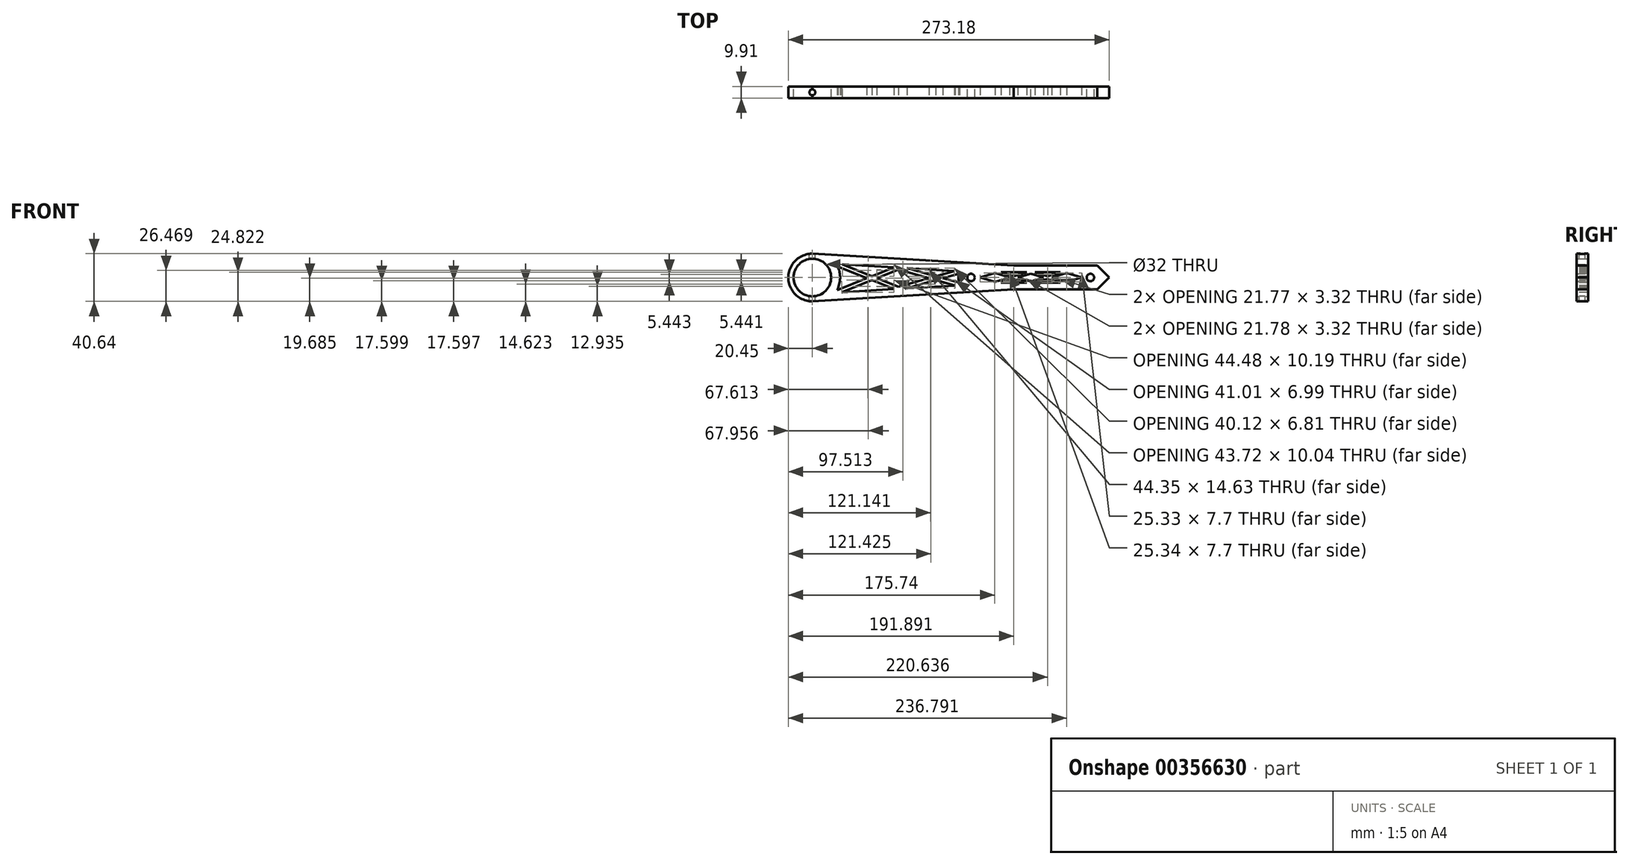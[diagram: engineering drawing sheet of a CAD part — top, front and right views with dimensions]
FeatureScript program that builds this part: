
annotation { "Feature Type Name" : "Feature", "Feature Type Description" : "" }
export const myFeature = defineFeature(function(context is Context, id is Id, definition is map)
    precondition{}
    {
        {
            var Q0;
            Q0=qCreatedBy(makeId("Front.planeOp"),FACE);
            var sketch = newSketch(context, id + "F0", { "sketchPlane" : qUnion([Q0])});
            skLineSegment(sketch, "E0.bottom", {"start": v(40.64, -10.16) * mm, "end": v(-40.64, -10.16) * mm});
            skLineSegment(sketch, "E0.top", {"start": v(40.64, 10.16) * mm, "end": v(-40.64, 10.16) * mm});
            skLineSegment(sketch, "E0.left", {"start": v(40.64, -10.16) * mm, "end": v(40.64, 10.16) * mm});
            skPoint(sketch, "E0.middle", {"position": v(0, 0) * mm});
            skLineSegment(sketch, "E1.bottom", {"start": v(-212.1, -20.32) * mm, "end": v(-212.36, -20.32) * mm});
            skLineSegment(sketch, "E1.top", {"start": v(-212.09, 20.32) * mm, "end": v(-212.36, 20.32) * mm});
            skLineSegment(sketch, "E1.right", {"start": v(-232.4, -2.34) * mm, "end": v(-232.4, 2.34) * mm});
            skPoint(sketch, "E1.middle", {"position": v(-212.1, 0) * mm});
            skCircle(sketch, "E2", {"center": v(-212.1, 0) * mm, "radius": 16 * mm});
            skArc(sketch, "E3", {"start": v(-212.09, 20.32) * mm, "mid": v(-232.54, 0) * mm, "end": v(-212.1, -20.32) * mm});
            skPoint(sketch, "E4.orphan", {"position": v(-232.4, 20.32) * mm});
            skPoint(sketch, "E5.orphan", {"position": v(-232.4, -20.32) * mm});
            skCircle(sketch, "E6", {"center": v(-77.09, 0) * mm, "radius": 3.18 * mm});
            skCircle(sketch, "E7", {"center": v(24.54, 0) * mm, "radius": 3.18 * mm});
            skLineSegment(sketch, "E8", {"start": v(-212.1, -20.32) * mm, "end": v(-40.64, -10.16) * mm});
            skLineSegment(sketch, "E9", {"start": v(-212.09, 20.32) * mm, "end": v(-40.64, 10.16) * mm});
            skLineSegment(sketch, "E10", {"start": v(-212.09, 31.09) * mm, "end": v(-212.09, -33.26) * mm, "construction": true});
            skSolve(sketch);
        }
        {
            var Q0;
            Q0 = qSketchRegion(id + "F0", true);
            extrude(context, id + "F1", {"entities" : qUnion([Q0]), "depth" : 9.9 * mm});
        }
        {
            var Q0;
            Q0=makeQuery(id+"F1.opExtrude","CAP_FACE",FACE,{"disambiguationData":[OSD([sQuery(id+"F0.wireOp",EDGE,"E0.bottom"),sQuery(id+"F0.wireOp",EDGE,"E0.top"),sQuery(id+"F0.wireOp",EDGE,"E0.left"),sQuery(id+"F0.wireOp",EDGE,"E2"),sQuery(id+"F0.wireOp",EDGE,"E3"),sQuery(id+"F0.wireOp",EDGE,"E6"),sQuery(id+"F0.wireOp",EDGE,"E7"),sQuery(id+"F0.wireOp",EDGE,"E8"),sQuery(id+"F0.wireOp",EDGE,"E9")])],"isStart":false});
            var sketch = newSketch(context, id + "F2", { "sketchPlane" : qUnion([Q0])});
            skArc(sketch, "E11.0", {"start": v(-192.22, -12.78) * mm, "mid": v(-188.48, -0.77) * mm, "end": v(-191.44, 11.46) * mm});
            skArc(sketch, "E12.0", {"start": v(-86.52, 5.25) * mm, "mid": v(-87.86, -0.73) * mm, "end": v(-85.73, -6.47) * mm});
            skLineSegment(sketch, "E13.0", {"start": v(-191.44, 11.46) * mm, "end": v(-86.52, 5.25) * mm});
            skLineSegment(sketch, "E14.0", {"start": v(-192.22, -12.78) * mm, "end": v(-85.73, -6.47) * mm});
            skSolve(sketch);
        }
        {
            var Q0;
            Q0 = qSketchRegion(id + "F2", true);
            extrude(context, id + "F3", {"entities" : qUnion([Q0]), "operationType" : NewBodyOperationType.REMOVE, "endBound" : BoundingType.THROUGH_ALL, "oppositeDirection" : true, "depth" : 25.4 * mm});
        }
        {
            var Q0;
            Q0=makeQuery(id+"F1.opExtrude","CAP_FACE",FACE,{"disambiguationData":[OSD([sQuery(id+"F0.wireOp",EDGE,"E0.bottom"),sQuery(id+"F0.wireOp",EDGE,"E0.top"),sQuery(id+"F0.wireOp",EDGE,"E0.left"),sQuery(id+"F0.wireOp",EDGE,"E2"),sQuery(id+"F0.wireOp",EDGE,"E3"),sQuery(id+"F0.wireOp",EDGE,"E6"),sQuery(id+"F0.wireOp",EDGE,"E7"),sQuery(id+"F0.wireOp",EDGE,"E8"),sQuery(id+"F0.wireOp",EDGE,"E9")])],"isStart":false});
            var sketch = newSketch(context, id + "F4", { "sketchPlane" : qUnion([Q0])});
            skLineSegment(sketch, "E15", {"start": v(-191.44, 11.46) * mm, "end": v(-138.98, -9.63) * mm});
            skLineSegment(sketch, "E16", {"start": v(-138.98, -9.63) * mm, "end": v(-86.52, 5.25) * mm});
            skLineSegment(sketch, "E17", {"start": v(-85.73, -6.47) * mm, "end": v(-138.98, 8.35) * mm});
            skLineSegment(sketch, "E18", {"start": v(-138.98, 8.35) * mm, "end": v(-192.22, -12.78) * mm});
            skLineSegment(sketch, "E19.0", {"start": v(-190.84, 12.94) * mm, "end": v(-138.39, -8.15) * mm});
            skLineSegment(sketch, "E20.0", {"start": v(-192.03, 9.99) * mm, "end": v(-139.57, -11.1) * mm});
            skLineSegment(sketch, "E21.0", {"start": v(-139.57, 9.83) * mm, "end": v(-192.81, -11.3) * mm});
            skLineSegment(sketch, "E22.0", {"start": v(-138.4, 6.88) * mm, "end": v(-191.64, -14.26) * mm});
            skLineSegment(sketch, "E23.0", {"start": v(-85.3, -4.94) * mm, "end": v(-138.55, 9.88) * mm});
            skLineSegment(sketch, "E24.0", {"start": v(-86.16, -8) * mm, "end": v(-139.4, 6.82) * mm});
            skLineSegment(sketch, "E25.0", {"start": v(-138.54, -11.15) * mm, "end": v(-86.1, 3.72) * mm});
            skLineSegment(sketch, "E26.0", {"start": v(-139.41, -8.1) * mm, "end": v(-86.96, 6.77) * mm});
            skLineSegment(sketch, "E27", {"start": v(-192.03, 9.99) * mm, "end": v(-190.84, 12.94) * mm});
            skSolve(sketch);
        }
        {
            var Q0;
            {var subQ0=sQuery(id+"F4.wireOp",EDGE,"E21.0");var subQ1=sQuery(id+"F4.wireOp",EDGE,"E15");var subQ2=makeQuery(id+"F4.imprint","INTERSECT",VERTEX,{"derivedFrom":[subQ1,subQ0]});Q0=makeQuery(id+"F4.imprint","IMPRINT",FACE,{"disambiguationData":[TD([[makeQuery(id+"F4.imprint","IMPRINT",EDGE,{"disambiguationData":[TD([[subQ2,-1.0]])],"derivedFrom":subQ1}),1.0]])]});}
            var Q1;
            {var subQ0=sQuery(id+"F4.wireOp",EDGE,"E21.0");var subQ1=sQuery(id+"F4.wireOp",EDGE,"E15");var subQ2=makeQuery(id+"F4.imprint","INTERSECT",VERTEX,{"derivedFrom":[subQ1,subQ0]});Q1=makeQuery(id+"F4.imprint","IMPRINT",FACE,{"disambiguationData":[TD([[makeQuery(id+"F4.imprint","IMPRINT",EDGE,{"disambiguationData":[TD([[subQ2,-1.0]])],"derivedFrom":subQ1}),-1.0]])]});}
            var Q2;
            {var subQ0=sQuery(id+"F4.wireOp",EDGE,"E18");var subQ1=sQuery(id+"F4.wireOp",EDGE,"E15");var subQ2=makeQuery(id+"F4.imprint","INTERSECT",VERTEX,{"derivedFrom":[subQ1,subQ0]});Q2=makeQuery(id+"F4.imprint","IMPRINT",FACE,{"disambiguationData":[TD([[makeQuery(id+"F4.imprint","IMPRINT",EDGE,{"disambiguationData":[TD([[subQ2,-1.0]])],"derivedFrom":subQ1}),1.0]])]});}
            var Q3;
            {var subQ0=sQuery(id+"F4.wireOp",EDGE,"E18");var subQ1=sQuery(id+"F4.wireOp",EDGE,"E15");var subQ2=makeQuery(id+"F4.imprint","INTERSECT",VERTEX,{"derivedFrom":[subQ1,subQ0]});Q3=makeQuery(id+"F4.imprint","IMPRINT",FACE,{"disambiguationData":[TD([[makeQuery(id+"F4.imprint","IMPRINT",EDGE,{"disambiguationData":[TD([[subQ2,-1.0]])],"derivedFrom":subQ1}),-1.0]])]});}
            var Q4;
            {var subQ0=sQuery(id+"F4.wireOp",EDGE,"E24.0");var subQ1=sQuery(id+"F4.wireOp",EDGE,"E16");var subQ2=makeQuery(id+"F4.imprint","INTERSECT",VERTEX,{"derivedFrom":[subQ1,subQ0]});Q4=makeQuery(id+"F4.imprint","IMPRINT",FACE,{"disambiguationData":[TD([[makeQuery(id+"F4.imprint","IMPRINT",EDGE,{"disambiguationData":[TD([[subQ2,-1.0]])],"derivedFrom":subQ1}),-1.0]])]});}
            var Q5;
            {var subQ0=sQuery(id+"F4.wireOp",EDGE,"E24.0");var subQ1=sQuery(id+"F4.wireOp",EDGE,"E16");var subQ2=makeQuery(id+"F4.imprint","INTERSECT",VERTEX,{"derivedFrom":[subQ1,subQ0]});Q5=makeQuery(id+"F4.imprint","IMPRINT",FACE,{"disambiguationData":[TD([[makeQuery(id+"F4.imprint","IMPRINT",EDGE,{"disambiguationData":[TD([[subQ2,-1.0]])],"derivedFrom":subQ1}),1.0]])]});}
            var Q6;
            {var subQ0=sQuery(id+"F4.wireOp",EDGE,"E17");var subQ1=sQuery(id+"F4.wireOp",EDGE,"E16");var subQ2=makeQuery(id+"F4.imprint","INTERSECT",VERTEX,{"derivedFrom":[subQ1,subQ0]});Q6=makeQuery(id+"F4.imprint","IMPRINT",FACE,{"disambiguationData":[TD([[makeQuery(id+"F4.imprint","IMPRINT",EDGE,{"disambiguationData":[TD([[subQ2,-1.0]])],"derivedFrom":subQ1}),-1.0]])]});}
            var Q7;
            {var subQ0=sQuery(id+"F4.wireOp",EDGE,"E17");var subQ1=sQuery(id+"F4.wireOp",EDGE,"E16");var subQ2=makeQuery(id+"F4.imprint","INTERSECT",VERTEX,{"derivedFrom":[subQ1,subQ0]});Q7=makeQuery(id+"F4.imprint","IMPRINT",FACE,{"disambiguationData":[TD([[makeQuery(id+"F4.imprint","IMPRINT",EDGE,{"disambiguationData":[TD([[subQ2,-1.0]])],"derivedFrom":subQ1}),1.0]])]});}
            var Q8;
            {var subQ3=sQuery(id+"F4.wireOp",EDGE,"E19.0");var subQ5=sQuery(id+"F4.wireOp",EDGE,"E26.0");var subQ6=makeQuery(id+"F4.imprint","INTERSECT",VERTEX,{"derivedFrom":[subQ3,subQ5]});Q8=makeQuery(id+"F4.imprint","IMPRINT",FACE,{"disambiguationData":[TD([[makeQuery(id+"F4.imprint","IMPRINT",EDGE,{"disambiguationData":[TD([[subQ6,1.0]])],"derivedFrom":subQ3}),-1.0]])]});}
            var Q9;
            {var subQ3=sQuery(id+"F4.wireOp",EDGE,"E19.0");var subQ5=sQuery(id+"F4.wireOp",EDGE,"E18");var subQ6=makeQuery(id+"F4.imprint","INTERSECT",VERTEX,{"derivedFrom":[subQ5,subQ3]});Q9=makeQuery(id+"F4.imprint","IMPRINT",FACE,{"disambiguationData":[TD([[makeQuery(id+"F4.imprint","IMPRINT",EDGE,{"disambiguationData":[TD([[subQ6,-1.0]])],"derivedFrom":subQ3}),1.0]])]});}
            var Q10;
            {var subQ0=sQuery(id+"F4.wireOp",EDGE,"E27");var subQ1=sQuery(id+"F4.wireOp",EDGE,"E19.0");var subQ2=makeQuery(id+"F4.imprint","INTERSECT",VERTEX,{"derivedFrom":[subQ1,subQ0]});Q10=makeQuery(id+"F4.imprint","IMPRINT",FACE,{"disambiguationData":[TD([[makeQuery(id+"F4.imprint","IMPRINT",EDGE,{"disambiguationData":[TD([[subQ2,-1.0]])],"derivedFrom":subQ1}),-1.0]])]});}
            var Q11;
            {var subQ0=sQuery(id+"F4.wireOp",EDGE,"E27");var subQ1=sQuery(id+"F4.wireOp",EDGE,"E20.0");var subQ2=makeQuery(id+"F4.imprint","INTERSECT",VERTEX,{"derivedFrom":[subQ1,subQ0]});Q11=makeQuery(id+"F4.imprint","IMPRINT",FACE,{"disambiguationData":[TD([[makeQuery(id+"F4.imprint","IMPRINT",EDGE,{"disambiguationData":[TD([[subQ2,-1.0]])],"derivedFrom":subQ1}),1.0]])]});}
            var Q12;
            {var subQ3=sQuery(id+"F4.wireOp",EDGE,"E21.0");var subQ5=sQuery(id+"F4.wireOp",EDGE,"E19.0");var subQ6=makeQuery(id+"F4.imprint","INTERSECT",VERTEX,{"derivedFrom":[subQ5,subQ3]});Q12=makeQuery(id+"F4.imprint","IMPRINT",FACE,{"disambiguationData":[TD([[makeQuery(id+"F4.imprint","IMPRINT",EDGE,{"disambiguationData":[TD([[subQ6,1.0]])],"derivedFrom":subQ5}),-1.0]])]});}
            var Q13;
            {var subQ0=sQuery(id+"F4.wireOp",EDGE,"E18");var subQ3=sQuery(id+"F4.wireOp",EDGE,"E20.0");var subQ4=makeQuery(id+"F4.imprint","INTERSECT",VERTEX,{"derivedFrom":[subQ0,subQ3]});Q13=makeQuery(id+"F4.imprint","IMPRINT",FACE,{"disambiguationData":[TD([[makeQuery(id+"F4.imprint","IMPRINT",EDGE,{"disambiguationData":[TD([[subQ4,1.0]])],"derivedFrom":subQ3}),-1.0]])]});}
            var Q14;
            {var subQ0=sQuery(id+"F4.wireOp",EDGE,"E18");var subQ3=sQuery(id+"F4.wireOp",EDGE,"E20.0");var subQ4=makeQuery(id+"F4.imprint","INTERSECT",VERTEX,{"derivedFrom":[subQ0,subQ3]});Q14=makeQuery(id+"F4.imprint","IMPRINT",FACE,{"disambiguationData":[TD([[makeQuery(id+"F4.imprint","IMPRINT",EDGE,{"disambiguationData":[TD([[subQ4,-1.0]])],"derivedFrom":subQ3}),-1.0]])]});}
            var Q15;
            {var subQ3=sQuery(id+"F4.wireOp",EDGE,"E26.0");var subQ5=sQuery(id+"F4.wireOp",EDGE,"E23.0");var subQ6=makeQuery(id+"F4.imprint","INTERSECT",VERTEX,{"derivedFrom":[subQ5,subQ3]});Q15=makeQuery(id+"F4.imprint","IMPRINT",FACE,{"disambiguationData":[TD([[makeQuery(id+"F4.imprint","IMPRINT",EDGE,{"disambiguationData":[TD([[subQ6,-1.0]])],"derivedFrom":subQ5}),1.0]])]});}
            var Q16;
            {var subQ0=sQuery(id+"F4.wireOp",EDGE,"E18");var subQ3=sQuery(id+"F4.wireOp",EDGE,"E19.0");var subQ4=makeQuery(id+"F4.imprint","INTERSECT",VERTEX,{"derivedFrom":[subQ0,subQ3]});Q16=makeQuery(id+"F4.imprint","IMPRINT",FACE,{"disambiguationData":[TD([[makeQuery(id+"F4.imprint","IMPRINT",EDGE,{"disambiguationData":[TD([[subQ4,1.0]])],"derivedFrom":subQ3}),1.0]])]});}
            var Q17;
            {var subQ0=sQuery(id+"F4.wireOp",EDGE,"E16");var subQ3=sQuery(id+"F4.wireOp",EDGE,"E23.0");var subQ4=makeQuery(id+"F4.imprint","INTERSECT",VERTEX,{"derivedFrom":[subQ0,subQ3]});Q17=makeQuery(id+"F4.imprint","IMPRINT",FACE,{"disambiguationData":[TD([[makeQuery(id+"F4.imprint","IMPRINT",EDGE,{"disambiguationData":[TD([[subQ4,1.0]])],"derivedFrom":subQ3}),-1.0]])]});}
            var Q18;
            {var subQ0=sQuery(id+"F4.wireOp",EDGE,"E16");var subQ3=sQuery(id+"F4.wireOp",EDGE,"E23.0");var subQ4=makeQuery(id+"F4.imprint","INTERSECT",VERTEX,{"derivedFrom":[subQ0,subQ3]});Q18=makeQuery(id+"F4.imprint","IMPRINT",FACE,{"disambiguationData":[TD([[makeQuery(id+"F4.imprint","IMPRINT",EDGE,{"disambiguationData":[TD([[subQ4,-1.0]])],"derivedFrom":subQ3}),-1.0]])]});}
            var Q19;
            {var subQ3=sQuery(id+"F4.wireOp",EDGE,"E25.0");var subQ5=sQuery(id+"F4.wireOp",EDGE,"E23.0");var subQ6=makeQuery(id+"F4.imprint","INTERSECT",VERTEX,{"derivedFrom":[subQ5,subQ3]});Q19=makeQuery(id+"F4.imprint","IMPRINT",FACE,{"disambiguationData":[TD([[makeQuery(id+"F4.imprint","IMPRINT",EDGE,{"disambiguationData":[TD([[subQ6,1.0]])],"derivedFrom":subQ5}),1.0]])]});}
            var Q20;
            {var subQ3=sQuery(id+"F4.wireOp",EDGE,"E25.0");var subQ5=sQuery(id+"F4.wireOp",EDGE,"E24.0");var subQ6=makeQuery(id+"F4.imprint","INTERSECT",VERTEX,{"derivedFrom":[subQ5,subQ3]});Q20=makeQuery(id+"F4.imprint","IMPRINT",FACE,{"disambiguationData":[TD([[makeQuery(id+"F4.imprint","IMPRINT",EDGE,{"disambiguationData":[TD([[subQ6,1.0]])],"derivedFrom":subQ5}),-1.0]])]});}
            var Q21;
            {var subQ0=sQuery(id+"F4.wireOp",EDGE,"E16");var subQ3=sQuery(id+"F4.wireOp",EDGE,"E24.0");var subQ4=makeQuery(id+"F4.imprint","INTERSECT",VERTEX,{"derivedFrom":[subQ0,subQ3]});Q21=makeQuery(id+"F4.imprint","IMPRINT",FACE,{"disambiguationData":[TD([[makeQuery(id+"F4.imprint","IMPRINT",EDGE,{"disambiguationData":[TD([[subQ4,1.0]])],"derivedFrom":subQ3}),1.0]])]});}
            var Q22;
            {var subQ3=sQuery(id+"F4.wireOp",EDGE,"E22.0");var subQ5=sQuery(id+"F4.wireOp",EDGE,"E20.0");var subQ6=makeQuery(id+"F4.imprint","INTERSECT",VERTEX,{"derivedFrom":[subQ5,subQ3]});Q22=makeQuery(id+"F4.imprint","IMPRINT",FACE,{"disambiguationData":[TD([[makeQuery(id+"F4.imprint","IMPRINT",EDGE,{"disambiguationData":[TD([[subQ6,-1.0]])],"derivedFrom":subQ5}),1.0]])]});}
            var Q23;
            {var subQ3=sQuery(id+"F4.wireOp",EDGE,"E21.0");var subQ5=sQuery(id+"F4.wireOp",EDGE,"E20.0");var subQ6=makeQuery(id+"F4.imprint","INTERSECT",VERTEX,{"derivedFrom":[subQ5,subQ3]});Q23=makeQuery(id+"F4.imprint","IMPRINT",FACE,{"disambiguationData":[TD([[makeQuery(id+"F4.imprint","IMPRINT",EDGE,{"disambiguationData":[TD([[subQ6,1.0]])],"derivedFrom":subQ5}),1.0]])]});}
            extrude(context, id + "F5", {"entities" : qUnion([Q0, Q1, Q2, Q3, Q4, Q5, Q6, Q7, Q8, Q9, Q10, Q11, Q12, Q13, Q14, Q15, Q16, Q17, Q18, Q19, Q20, Q21, Q22, Q23]), "operationType" : NewBodyOperationType.ADD, "oppositeDirection" : true, "depth" : 9.9 * mm});
        }
        {
            var Q0;
            Q0=makeQuery(id+"F5.boolean.opBoolean","MERGE",FACE,{"derivedFrom":[makeQuery(id+"F1.opExtrude","CAP_FACE",FACE,{"disambiguationData":[OSD([sQuery(id+"F0.wireOp",EDGE,"E0.bottom"),sQuery(id+"F0.wireOp",EDGE,"E0.top"),sQuery(id+"F0.wireOp",EDGE,"E0.left"),sQuery(id+"F0.wireOp",EDGE,"E2"),sQuery(id+"F0.wireOp",EDGE,"E3"),sQuery(id+"F0.wireOp",EDGE,"E6"),sQuery(id+"F0.wireOp",EDGE,"E7"),sQuery(id+"F0.wireOp",EDGE,"E8"),sQuery(id+"F0.wireOp",EDGE,"E9")])],"isStart":false}),makeQuery(id+"F5.opExtrude","CAP_FACE",FACE,{"disambiguationData":[OSD([sQuery(id+"F2.wireOp",EDGE,"E11.0"),sQuery(id+"F2.wireOp",EDGE,"E12.0"),sQuery(id+"F2.wireOp",EDGE,"E13.0"),sQuery(id+"F2.wireOp",EDGE,"E14.0"),sQuery(id+"F4.wireOp",EDGE,"E19.0"),sQuery(id+"F4.wireOp",EDGE,"E20.0"),sQuery(id+"F4.wireOp",EDGE,"E21.0"),sQuery(id+"F4.wireOp",EDGE,"E22.0"),sQuery(id+"F4.wireOp",EDGE,"E23.0"),sQuery(id+"F4.wireOp",EDGE,"E24.0"),sQuery(id+"F4.wireOp",EDGE,"E25.0"),sQuery(id+"F4.wireOp",EDGE,"E26.0"),sQuery(id+"F4.wireOp",EDGE,"E27")])],"isStart":true})]});
            var sketch = newSketch(context, id + "F6", { "sketchPlane" : qUnion([Q0])});
            skLineSegment(sketch, "E28.0.left", {"start": v(-55.02, 4.38) * mm, "end": v(2.47, 4.38) * mm});
            skLineSegment(sketch, "E28.0.right", {"start": v(-55.02, -4.38) * mm, "end": v(2.47, -4.38) * mm});
            skLineSegment(sketch, "E29", {"start": v(-55.02, -4.38) * mm, "end": v(-69.47, 0) * mm});
            skLineSegment(sketch, "E30", {"start": v(-69.47, 0) * mm, "end": v(-55.02, 4.38) * mm});
            skLineSegment(sketch, "E31", {"start": v(2.47, 4.38) * mm, "end": v(16.92, 0) * mm});
            skLineSegment(sketch, "E32", {"start": v(16.92, 0) * mm, "end": v(2.47, -4.38) * mm});
            skLineSegment(sketch, "E33", {"start": v(-26.28, 4.38) * mm, "end": v(-55.02, -4.38) * mm});
            skLineSegment(sketch, "E34", {"start": v(-55.02, 4.38) * mm, "end": v(-26.28, -4.38) * mm});
            skLineSegment(sketch, "E35", {"start": v(-26.28, -4.38) * mm, "end": v(-26.28, 4.38) * mm});
            skLineSegment(sketch, "E36", {"start": v(2.47, -4.38) * mm, "end": v(-26.28, 4.38) * mm});
            skLineSegment(sketch, "E37", {"start": v(-26.28, -4.38) * mm, "end": v(2.47, 4.38) * mm});
            skLineSegment(sketch, "E38.0", {"start": v(-27.3, 5.13) * mm, "end": v(-56.77, -3.85) * mm});
            skLineSegment(sketch, "E39.0", {"start": v(-22.8, 4.38) * mm, "end": v(-57.09, -6.07) * mm});
            skLineSegment(sketch, "E40.0", {"start": v(-56.77, 3.85) * mm, "end": v(-27.3, -5.13) * mm});
            skLineSegment(sketch, "E41.0", {"start": v(4.22, -3.85) * mm, "end": v(-26.64, 5.55) * mm});
            skLineSegment(sketch, "E42.0", {"start": v(3.15, -5.65) * mm, "end": v(-27.24, 3.6) * mm});
            skLineSegment(sketch, "E43.0", {"start": v(-26.64, -5.55) * mm, "end": v(4.22, 3.85) * mm});
            skLineSegment(sketch, "E44.0", {"start": v(-27.24, -3.61) * mm, "end": v(3.15, 5.65) * mm});
            skLineSegment(sketch, "E45.0", {"start": v(-57.09, 6.07) * mm, "end": v(-22.8, -4.38) * mm});
            skLineSegment(sketch, "E46", {"start": v(-56.77, -3.85) * mm, "end": v(-56.77, 3.85) * mm});
            skLineSegment(sketch, "E47", {"start": v(4.22, 3.85) * mm, "end": v(4.22, -3.85) * mm});
            skSolve(sketch);
        }
        {
            var Q0;
            {var subQ0=sQuery(id+"F6.wireOp",EDGE,"05a44146-ae9a-411f-92ef-b6872708c7e9.0");var subQ1=sQuery(id+"F6.wireOp",EDGE,"E28.0.left");var subQ2=makeQuery(id+"F6.imprint","INTERSECT",VERTEX,{"derivedFrom":[subQ1,subQ0]});Q0=makeQuery(id+"F6.imprint","IMPRINT",FACE,{"disambiguationData":[TD([[makeQuery(id+"F6.imprint","IMPRINT",EDGE,{"disambiguationData":[TD([[subQ2,-1.0]])],"derivedFrom":subQ1}),-1.0]])]});}
            var Q1;
            {var subQ0=sQuery(id+"F6.wireOp",EDGE,"E39.0");var subQ1=sQuery(id+"F6.wireOp",EDGE,"E28.0.right");var subQ2=makeQuery(id+"F6.imprint","INTERSECT",VERTEX,{"derivedFrom":[subQ1,subQ0]});Q1=makeQuery(id+"F6.imprint","IMPRINT",FACE,{"disambiguationData":[TD([[makeQuery(id+"F6.imprint","IMPRINT",EDGE,{"disambiguationData":[TD([[subQ2,-1.0]])],"derivedFrom":subQ1}),1.0]])]});}
            var Q2;
            {var subQ0=sQuery(id+"F6.wireOp",EDGE,"05a44146-ae9a-411f-92ef-b6872708c7e9.0");var subQ1=sQuery(id+"F6.wireOp",EDGE,"E35");var subQ2=makeQuery(id+"F6.imprint","INTERSECT",VERTEX,{"derivedFrom":[subQ1,subQ0]});Q2=makeQuery(id+"F6.imprint","IMPRINT",FACE,{"disambiguationData":[TD([[makeQuery(id+"F6.imprint","IMPRINT",EDGE,{"disambiguationData":[TD([[subQ2,1.0]])],"derivedFrom":subQ0}),1.0]])]});}
            var Q3;
            {var subQ0=sQuery(id+"F6.wireOp",EDGE,"c7637492-37e4-4d5e-8088-8b7a20f406ff.0");var subQ1=sQuery(id+"F6.wireOp",EDGE,"E28.0.right");var subQ2=makeQuery(id+"F6.imprint","INTERSECT",VERTEX,{"derivedFrom":[subQ1,subQ0]});Q3=makeQuery(id+"F6.imprint","IMPRINT",FACE,{"disambiguationData":[TD([[makeQuery(id+"F6.imprint","IMPRINT",EDGE,{"disambiguationData":[TD([[subQ2,-1.0]])],"derivedFrom":subQ1}),1.0]])]});}
            var Q4;
            {var subQ1=sQuery(id+"F6.wireOp",EDGE,"E28.0.left");var subQ3=sQuery(id+"F6.wireOp",EDGE,"E41.0");var subQ4=makeQuery(id+"F6.imprint","INTERSECT",VERTEX,{"derivedFrom":[subQ1,subQ3]});Q4=makeQuery(id+"F6.imprint","IMPRINT",FACE,{"disambiguationData":[TD([[makeQuery(id+"F6.imprint","IMPRINT",EDGE,{"disambiguationData":[TD([[subQ4,1.0]])],"derivedFrom":subQ3}),-1.0]])]});}
            var Q5;
            {var subQ0=sQuery(id+"F6.wireOp",EDGE,"E42.0");var subQ3=sQuery(id+"F6.wireOp",EDGE,"E44.0");var subQ5=makeQuery(id+"F6.imprint","INTERSECT",VERTEX,{"derivedFrom":[subQ0,subQ3]});Q5=makeQuery(id+"F6.imprint","IMPRINT",FACE,{"disambiguationData":[TD([[makeQuery(id+"F6.imprint","IMPRINT",EDGE,{"disambiguationData":[TD([[subQ5,-1.0]])],"derivedFrom":subQ0}),1.0]])]});}
            var Q6;
            {var subQ1=sQuery(id+"F6.wireOp",EDGE,"E28.0.right");var subQ3=sQuery(id+"F6.wireOp",EDGE,"E42.0");var subQ4=makeQuery(id+"F6.imprint","INTERSECT",VERTEX,{"derivedFrom":[subQ1,subQ3]});Q6=makeQuery(id+"F6.imprint","IMPRINT",FACE,{"disambiguationData":[TD([[makeQuery(id+"F6.imprint","IMPRINT",EDGE,{"disambiguationData":[TD([[subQ4,-1.0]])],"derivedFrom":subQ3}),1.0]])]});}
            var Q7;
            {var subQ0=sQuery(id+"F6.wireOp",EDGE,"E45.0");var subQ3=sQuery(id+"F6.wireOp",EDGE,"E39.0");var subQ5=makeQuery(id+"F6.imprint","INTERSECT",VERTEX,{"derivedFrom":[subQ3,subQ0]});Q7=makeQuery(id+"F6.imprint","IMPRINT",FACE,{"disambiguationData":[TD([[makeQuery(id+"F6.imprint","IMPRINT",EDGE,{"disambiguationData":[TD([[subQ5,1.0]])],"derivedFrom":subQ3}),1.0]])]});}
            var Q8;
            {var subQ3=sQuery(id+"F6.wireOp",EDGE,"E46");Q8=makeQuery(id+"F6.imprint","IMPRINT",FACE,{"disambiguationData":[TD([[makeQuery(id+"F6.imprint","IMPRINT",EDGE,{"derivedFrom":subQ3}),1.0]])]});}
            var Q9;
            {var subQ0=sQuery(id+"F6.wireOp",EDGE,"E46");Q9=makeQuery(id+"F6.imprint","IMPRINT",FACE,{"disambiguationData":[TD([[makeQuery(id+"F6.imprint","IMPRINT",EDGE,{"derivedFrom":subQ0}),-1.0]])]});}
            var Q10;
            {var subQ0=sQuery(id+"F6.wireOp",EDGE,"E47");Q10=makeQuery(id+"F6.imprint","IMPRINT",FACE,{"disambiguationData":[TD([[makeQuery(id+"F6.imprint","IMPRINT",EDGE,{"derivedFrom":subQ0}),-1.0]])]});}
            var Q11;
            {var subQ3=sQuery(id+"F6.wireOp",EDGE,"E47");Q11=makeQuery(id+"F6.imprint","IMPRINT",FACE,{"disambiguationData":[TD([[makeQuery(id+"F6.imprint","IMPRINT",EDGE,{"derivedFrom":subQ3}),1.0]])]});}
            var Q12;
            {var subQ0=sQuery(id+"F6.wireOp",EDGE,"E35");var subQ1=makeQuery(id+"F6.imprint","INTERSECT",VERTEX,{"derivedFrom":[subQ0,sQuery(id+"F6.wireOp",EDGE,"E44.0")]});Q12=makeQuery(id+"F6.imprint","IMPRINT",FACE,{"disambiguationData":[TD([[makeQuery(id+"F6.imprint","IMPRINT",EDGE,{"disambiguationData":[TD([[subQ1,-1.0]])],"derivedFrom":subQ0}),1.0]])]});}
            extrude(context, id + "F7", {"entities" : qUnion([Q0, Q1, Q2, Q3, Q4, Q5, Q6, Q7, Q8, Q9, Q10, Q11, Q12]), "operationType" : NewBodyOperationType.REMOVE, "oppositeDirection" : true, "depth" : 25.4 * mm});
        }
        {
            var Q0;
            Q0=makeQuery(id+"F1.opExtrude","SWEPT_EDGE",EDGE,{"disambiguationData":[OSD([sQuery(id+"F0.wireOp",EDGE,"E0.bottom"),sQuery(id+"F0.wireOp",EDGE,"E0.left")])]});
            var Q1;
            Q1=makeQuery(id+"F1.opExtrude","SWEPT_EDGE",EDGE,{"disambiguationData":[OSD([sQuery(id+"F0.wireOp",EDGE,"E0.top"),sQuery(id+"F0.wireOp",EDGE,"E0.left")])]});
            chamfer(context, id + "F8", {"entities" : qUnion([Q0, Q1]), "width" : 10.16 * mm, "tangentPropagation" : true});
        }
        {
            var Q0;
            Q0=qCreatedBy(makeId("Top.planeOp"),FACE);
            var sketch = newSketch(context, id + "F9", { "sketchPlane" : qUnion([Q0])});
            skCircle(sketch, "E48", {"center": v(-212.1, -4.95) * mm, "radius": 2.54 * mm});
            skSolve(sketch);
        }
        {
            var Q0;
            Q0 = qSketchRegion(id + "F9", true);
            extrude(context, id + "F10", {"entities" : qUnion([Q0]), "operationType" : NewBodyOperationType.REMOVE, "oppositeDirection" : true, "depth" : 127 * mm, "symmetric" : true});
        }
    });
